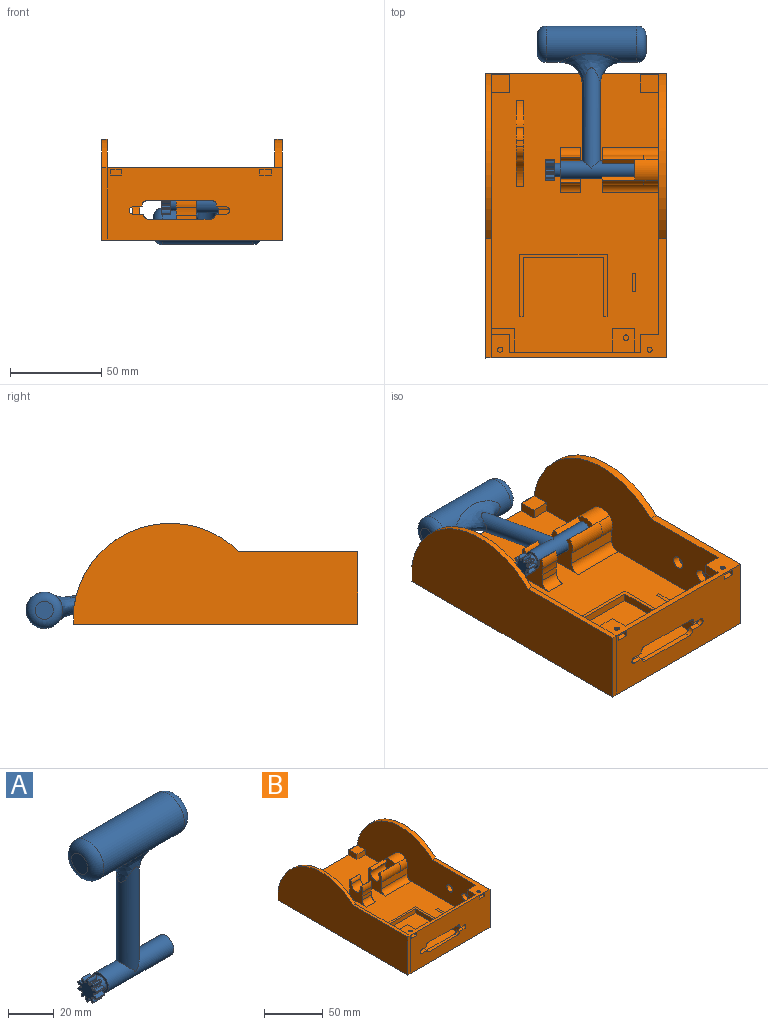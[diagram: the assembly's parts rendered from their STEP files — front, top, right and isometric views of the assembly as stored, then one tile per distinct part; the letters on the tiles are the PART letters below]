
ASSEMBLY  parts=2 mates=1
PART A: 72 faces, bbox 59.7x21.6x87 mm
  f0: cylinder r=5mm len=56.08mm, axis (0,0,-1), area 1528.4mm2, adj f1,f5
  f1: cylinder r=5mm len=40.5mm, axis (-1,0,0), area 1172.3mm2, adj f0,f4,f68
  f2: cylinder r=10mm len=49.7mm, axis (-1,0,0), area 2668.9mm2, adj f5,f70,f71
  f3: plane 10x10mm, normal (1,0,0), area 78.5mm2, adj f71
  f4: plane 10x10mm, normal (-1,0,0), area 34.4mm2, adj f1,f6
  f5: bspline ~34.02x15.67mm, area 649.5mm2, adj f0,f2
  f6: cylinder r=3.75mm len=8.13mm, axis (1,0,0), area 89.7mm2, adj f4,f7,f8,f9,f10,f11,f12,f13
  f7: plane 2.7x2.45mm, normal (1,0,0), area 3.1mm2, adj f6,f21,f40,f42,f45,f47
  f8: plane 2.4x2.01mm, normal (1,0,0), area 3.1mm2, adj f6,f20,f44,f46,f49,f51
  f9: plane 2.7x2.45mm, normal (1,0,0), area 3.1mm2, adj f6,f24,f33,f35,f48,f50
  f10: plane 2.68x2.12mm, normal (1,0,0), area 3.1mm2, adj f6,f26,f29,f31,f32,f34
  f11: plane 2.68x2.12mm, normal (1,0,0), area 3.1mm2, adj f6,f17,f28,f30,f61,f63
  f12: plane 2.7x2.45mm, normal (1,0,0), area 3.1mm2, adj f6,f16,f60,f62,f65,f67
  f13: plane 2.4x2.01mm, normal (1,0,0), area 3.1mm2, adj f6,f19,f53,f55,f64,f66
  f14: plane 2.7x2.45mm, normal (1,0,0), area 3.1mm2, adj f6,f18,f52,f54,f57,f59
  f15: plane 2.68x2.12mm, normal (1,0,0), area 3.1mm2, adj f6,f23,f37,f39,f56,f58
  f16: cylinder r=6mm len=5mm, axis (1,0,0), area 2.9mm2, adj f12,f25,f60,f65
  f17: cylinder r=6mm len=5mm, axis (1,0,0), area 2.9mm2, adj f11,f25,f28,f61
  f18: cylinder r=6mm len=5mm, axis (1,0,0), area 2.9mm2, adj f14,f25,f52,f57
  f19: cylinder r=6mm len=5mm, axis (1,0,0), area 2.9mm2, adj f13,f25,f53,f64
  f20: cylinder r=6mm len=5mm, axis (1,0,0), area 2.9mm2, adj f8,f25,f44,f49
  f21: cylinder r=6mm len=5mm, axis (1,0,0), area 2.9mm2, adj f7,f25,f40,f45
  f22: cylinder r=6mm len=5mm, axis (1,0,0), area 2.9mm2, adj f25,f27,f36,f41
  f23: cylinder r=6mm len=5mm, axis (1,0,0), area 2.9mm2, adj f15,f25,f37,f56
  f24: cylinder r=6mm len=5mm, axis (1,0,0), area 2.9mm2, adj f9,f25,f33,f48
  f25: plane 12.02x11.61mm, normal (-1,0,0), area 75.1mm2, adj f6,f16,f17,f18,f19,f20,f21,f22
  f26: cylinder r=6mm len=5mm, axis (1,0,0), area 2.9mm2, adj f10,f25,f29,f32
  f27: plane 2.68x2.12mm, normal (1,0,0), area 3.1mm2, adj f6,f22,f36,f38,f41,f43
  f28: extruded ~5x1.69mm, area 10.2mm2, adj f11,f17,f25,f30
  f29: extruded ~5x1.69mm, area 10.2mm2, adj f10,f25,f26,f31
  f30: cylinder r=0.41mm len=5mm, axis (1,0,0), area 3mm2, adj f6,f11,f25,f28
  f31: cylinder r=0.41mm len=5mm, axis (1,0,0), area 3mm2, adj f6,f10,f25,f29
  f32: extruded ~5x1.95mm, area 10.2mm2, adj f10,f25,f26,f34
  f33: extruded ~5x1.79mm, area 10.2mm2, adj f9,f24,f25,f35
  f34: cylinder r=0.41mm len=5mm, axis (1,0,0), area 3mm2, adj f6,f10,f25,f32
  f35: cylinder r=0.41mm len=5mm, axis (1,0,0), area 3mm2, adj f6,f9,f25,f33
  f36: extruded ~5x1.69mm, area 10.2mm2, adj f22,f25,f27,f38
  f37: extruded ~5x1.69mm, area 10.2mm2, adj f15,f23,f25,f39
  f38: cylinder r=0.41mm len=5mm, axis (1,0,0), area 3mm2, adj f6,f25,f27,f36
  f39: cylinder r=0.41mm len=5mm, axis (1,0,0), area 3mm2, adj f6,f15,f25,f37
  f40: extruded ~5x1.79mm, area 10.2mm2, adj f7,f21,f25,f42
  f41: extruded ~5x1.95mm, area 10.2mm2, adj f22,f25,f27,f43
  f42: cylinder r=0.41mm len=5mm, axis (1,0,0), area 3mm2, adj f6,f7,f25,f40
  f43: cylinder r=0.41mm len=5mm, axis (1,0,0), area 3mm2, adj f6,f25,f27,f41
  f44: extruded ~5x1.91mm, area 10.2mm2, adj f8,f20,f25,f46
  f45: extruded ~5x1.46mm, area 10.2mm2, adj f7,f21,f25,f47
  f46: cylinder r=0.41mm len=5mm, axis (1,0,0), area 3mm2, adj f6,f8,f25,f44
  f47: cylinder r=0.41mm len=5mm, axis (1,0,0), area 3mm2, adj f6,f7,f25,f45
  f48: extruded ~5x1.46mm, area 10.2mm2, adj f9,f24,f25,f50
  f49: extruded ~5x1.91mm, area 10.2mm2, adj f8,f20,f25,f51
  f50: cylinder r=0.41mm len=5mm, axis (1,0,0), area 3mm2, adj f6,f9,f25,f48
  f51: cylinder r=0.41mm len=5mm, axis (1,0,0), area 3mm2, adj f6,f8,f25,f49
  f52: extruded ~5x1.46mm, area 10.2mm2, adj f14,f18,f25,f54
  f53: extruded ~5x1.91mm, area 10.2mm2, adj f13,f19,f25,f55
  f54: cylinder r=0.41mm len=5mm, axis (1,0,0), area 3mm2, adj f6,f14,f25,f52
  f55: cylinder r=0.41mm len=5mm, axis (1,0,0), area 3mm2, adj f6,f13,f25,f53
  f56: extruded ~5x1.95mm, area 10.2mm2, adj f15,f23,f25,f58
  f57: extruded ~5x1.79mm, area 10.2mm2, adj f14,f18,f25,f59
  f58: cylinder r=0.41mm len=5mm, axis (1,0,0), area 3mm2, adj f6,f15,f25,f56
  f59: cylinder r=0.41mm len=5mm, axis (1,0,0), area 3mm2, adj f6,f14,f25,f57
  f60: extruded ~5x1.79mm, area 10.2mm2, adj f12,f16,f25,f62
  f61: extruded ~5x1.95mm, area 10.2mm2, adj f11,f17,f25,f63
  f62: cylinder r=0.41mm len=5mm, axis (1,0,0), area 3mm2, adj f6,f12,f25,f60
  f63: cylinder r=0.41mm len=5mm, axis (1,0,0), area 3mm2, adj f6,f11,f25,f61
  f64: extruded ~5x1.91mm, area 10.2mm2, adj f13,f19,f25,f66
  f65: extruded ~5x1.46mm, area 10.2mm2, adj f12,f16,f25,f67
  f66: cylinder r=0.41mm len=5mm, axis (1,0,0), area 3mm2, adj f6,f13,f25,f64
  f67: cylinder r=0.41mm len=5mm, axis (1,0,0), area 3mm2, adj f6,f12,f25,f65
  f68: plane 10x10mm, normal (1,0,0), area 78.5mm2, adj f1
  f69: plane 10x10mm, normal (-1,0,0), area 78.5mm2, adj f70
  f70: torus R=5mm, axis (1,0,0), area 403.8mm2, adj f2,f69
  f71: torus R=5mm, axis (1,0,0), area 403.8mm2, adj f2,f3
PART B: 146 faces, bbox 99.2x155.8x55.3 mm
  f0: plane 96.21x39.7mm, normal (0,-1,0), area 3329.3mm2, adj f3,f4,f18,f37,f56,f57,f58,f59
  f1: plane 152.74x50.32mm, normal (-1,0,0), area 5424.2mm2, adj f2,f15,f20,f21,f22,f23,f24,f25
  f2: plane 91.94x34.7mm, normal (0,1,0), area 2463.3mm2, adj f1,f16,f37,f56,f57,f58,f59,f60
  f3: plane 11x3mm, normal (-1,0,0), area 33mm2, adj f0,f90,f141,f145
  f4: plane 11x3mm, normal (-1,0,0), area 33mm2, adj f0,f89,f140,f144
  f5: plane 155.76x55.32mm, normal (-1,0,0), area 6830mm2, adj f68,f69,f70,f71,f97,f136
  f6: plane 24.89x19.22mm, normal (1,0,0), area 214.8mm2, adj f7,f8,f17,f28,f29,f40,f41,f119
  f7: cylinder r=8.15mm len=11mm, axis (-1,0,0), area 69mm2, adj f6,f9,f127,f131
  f8: cylinder r=5.15mm len=11mm, axis (-1,0,0), area 188.3mm2, adj f6,f9,f128,f129
  f9: plane 24.89x19.22mm, normal (-1,0,0), area 214.8mm2, adj f7,f8,f17,f28,f29,f40,f41,f119
  f10: plane 10.2x3.5mm, normal (-1,0,0), area 35.7mm2, adj f116,f118,f119,f123
  f11: plane 10.2x3.5mm, normal (1,0,0), area 35.7mm2, adj f116,f118,f119,f123
  f12: plane 6.6x3.5mm, normal (0,1,0), area 23.1mm2, adj f119,f120,f121,f122
  f13: plane 12.95x6.5mm, normal (0,1,0), area 61.1mm2, adj f16,f102,f103,f119,f120,f121,f122
  f14: plane 10x5.5mm, normal (0,1,0), area 55mm2, adj f16,f37,f76,f142
  f15: plane 10x5.5mm, normal (0,1,0), area 55mm2, adj f1,f37,f77,f143
  f16: plane 152.73x50.32mm, normal (1,0,0), area 5755mm2, adj f2,f13,f14,f68,f70,f75,f103,f119
  f17: cylinder r=8.15mm len=11mm, axis (-1,0,0), area 69mm2, adj f6,f9,f126,f130
  f18: plane 155.76x55.32mm, normal (1,0,0), area 6753.1mm2, adj f0,f36,f37,f42,f43,f71,f97
  f19: plane 4x3mm, normal (0,0,1), area 12mm2, adj f50,f51,f54,f55
  f20: cylinder r=9mm len=13.11mm, axis (-1,0,0), area 163.9mm2, adj f1,f21,f22,f30,f31,f38
  f21: cylinder r=8.1mm len=9.08mm, axis (-1,0,0), area 79.7mm2, adj f1,f20,f23,f39
  f22: cylinder r=8.2mm len=9.08mm, axis (-1,0,0), area 79.5mm2, adj f1,f20,f24,f27
  f23: plane 30.94x6.68mm, normal (0,1,0), area 206.7mm2, adj f1,f21,f25,f31,f35
  f24: plane 30.94x6.68mm, normal (0,-1,0), area 206.7mm2, adj f1,f22,f26,f30,f35
  f25: cylinder r=5mm len=30.94mm, axis (1,0,0), area 243mm2, adj f1,f23,f35,f119
  f26: cylinder r=5mm len=30.94mm, axis (-1,0,0), area 243mm2, adj f1,f24,f35,f119
  f27: plane 9.08x2.39mm, normal (1,0,0), area 0.1mm2, adj f22,f30
  f28: plane 11x3.73mm, normal (0,-1,0), area 41.1mm2, adj f6,f9,f40,f130
  f29: plane 11x3.73mm, normal (0,1,0), area 41.1mm2, adj f6,f9,f41,f131
  f30: cylinder r=8.15mm len=22.84mm, axis (-1,0,0), area 224.3mm2, adj f20,f24,f27,f34,f35
  f31: cylinder r=8.15mm len=22.84mm, axis (-1,0,0), area 224.3mm2, adj f20,f23,f32,f35,f39
  f32: plane 17.84x2.12mm, normal (0,-0.71,0.71), area 53.5mm2, adj f31,f33,f35,f38
  f33: cylinder r=5.15mm len=17.84mm, axis (-1,0,0), area 432.9mm2, adj f32,f34,f35,f38
  f34: plane 17.84x2.12mm, normal (0,0.71,0.71), area 53.5mm2, adj f30,f33,f35,f38
  f35: plane 24.89x20.76mm, normal (-1,0,0), area 226.9mm2, adj f23,f24,f25,f26,f30,f31,f32,f33
  f36: cylinder r=53.32mm len=90.46mm, axis (1,0,0), area 502.6mm2, adj f1,f18,f37,f71,f132
  f37: plane 96.21x65.3mm, normal (0,0,1), area 741.9mm2, adj f0,f1,f2,f14,f15,f18,f36,f70
  f38: plane 13x11.53mm, normal (-1,0,0), area 112.2mm2, adj f20,f32,f33,f34
  f39: plane 9.08x2.4mm, normal (-1,0,0), area 0.1mm2, adj f21,f31
  f40: cylinder r=5mm len=11mm, axis (-1,0,0), area 86.4mm2, adj f6,f9,f28,f119
  f41: cylinder r=5mm len=11mm, axis (1,0,0), area 86.4mm2, adj f6,f9,f29,f119
  f42: cylinder r=3.5mm len=7mm, axis (1,0,0), area 93.8mm2, adj f1,f18
  f43: cylinder r=3.5mm len=7mm, axis (1,0,0), area 93.8mm2, adj f1,f18
  f44: plane 9x4mm, normal (0,1,0), area 36mm2, adj f50,f52,f54,f55
  f45: plane 9x4mm, normal (0,-1,0), area 36mm2, adj f51,f53,f54,f55
  f46: cylinder r=4.05mm len=8.1mm, axis (1,0,0), area 50.9mm2, adj f47,f49,f54,f55
  f47: plane 16x4mm, normal (0,-1,0), area 64mm2, adj f46,f48,f54,f55
  f48: cylinder r=4.05mm len=8.1mm, axis (1,0,0), area 50.9mm2, adj f47,f49,f54,f55
  f49: plane 16x4mm, normal (0,1,0), area 64mm2, adj f46,f48,f54,f55
  f50: cylinder r=7mm len=7mm, axis (1,0,0), area 44mm2, adj f19,f44,f54,f55
  f51: cylinder r=7mm len=7mm, axis (-1,0,0), area 44mm2, adj f19,f45,f54,f55
  f52: cylinder r=15mm len=15mm, axis (-1,0,0), area 94.2mm2, adj f44,f54,f55,f119
  f53: cylinder r=15mm len=15mm, axis (1,0,0), area 94.2mm2, adj f45,f54,f55,f119
  f54: plane 47x31mm, normal (1,0,0), area 421.4mm2, adj f19,f44,f45,f46,f47,f48,f49,f50
  f55: plane 47x31mm, normal (-1,0,0), area 421.4mm2, adj f19,f44,f45,f46,f47,f48,f49,f50
  f56: plane 36.58x3mm, normal (0,0,-1), area 109.7mm2, adj f0,f2,f98,f99
  f57: plane 3x1.08mm, normal (-1,0,0.1), area 3.3mm2, adj f0,f2,f58,f98
  f58: plane 5.71x3mm, normal (0,0,-1), area 17.1mm2, adj f0,f2,f57,f59
  f59: cylinder r=2mm len=3.99mm, axis (0,1,0), area 18.9mm2, adj f0,f2,f58,f60
  f60: plane 5.5x3mm, normal (0,0,1), area 16.5mm2, adj f0,f2,f59,f61
  f61: plane 3x0.07mm, normal (-1,0,0.1), area 0.2mm2, adj f0,f2,f60,f100
  f62: plane 33.57x3mm, normal (0,0,1), area 100.7mm2, adj f0,f2,f100,f101
  f63: plane 3x0.07mm, normal (1,0,0.1), area 0.2mm2, adj f0,f2,f64,f101
  f64: plane 5.5x3mm, normal (0,0,1), area 16.5mm2, adj f0,f2,f63,f65
  f65: cylinder r=2mm len=3.99mm, axis (0,1,0), area 18.9mm2, adj f0,f2,f64,f66
  f66: plane 5.71x3mm, normal (0,0,-1), area 17.1mm2, adj f0,f2,f65,f67
  f67: plane 3x1.05mm, normal (1,0,0.1), area 3.2mm2, adj f0,f2,f66,f99
  f68: cylinder r=53.32mm len=90.46mm, axis (1,0,0), area 353.7mm2, adj f5,f16,f70,f134,f136
  f69: plane 39.7x3mm, normal (0,-1,0), area 119.1mm2, adj f0,f5,f70,f97
  f70: plane 65.3x3mm, normal (0,0,1), area 195.9mm2, adj f5,f16,f37,f68,f69
  f71: plane 99.21x9.71mm, normal (0,1,0), area 612.1mm2, adj f5,f18,f36,f72,f74,f95,f96,f97
  f72: plane 10x5.21mm, normal (-1,0,0), area 52mm2, adj f71,f73,f119,f133,f138
  f73: plane 10x5.21mm, normal (0,-1,0), area 52.1mm2, adj f1,f72,f119,f133
  f74: plane 10x5.21mm, normal (1,0,0), area 52mm2, adj f71,f75,f119,f135,f137
  f75: plane 10x5.21mm, normal (0,-1,0), area 52.1mm2, adj f16,f74,f119,f135
  f76: plane 10x5.5mm, normal (1,0,0), area 55mm2, adj f2,f14,f37,f142
  f77: plane 10x5.5mm, normal (-1,0,0), area 55mm2, adj f2,f15,f37,f143
  f78: plane 11x3mm, normal (1,0,0), area 33mm2, adj f0,f90,f141,f145
  f79: plane 11x3mm, normal (1,0,0), area 33mm2, adj f0,f89,f139,f144
  f80: plane 8.71x3.21mm, normal (0,-1,0), area 24.8mm2, adj f81,f84,f91,f96,f97
  f81: plane 8.71x3.2mm, normal (0,-1,0), area 24.8mm2, adj f80,f82,f91,f96,f97
  f82: plane 8.71x2.99mm, normal (1,0,0), area 26.1mm2, adj f81,f83,f91,f97
  f83: plane 8.71x6.4mm, normal (0,1,0), area 55.7mm2, adj f82,f84,f91,f97
  f84: plane 8.71x3mm, normal (-1,0,0), area 26.1mm2, adj f80,f83,f91,f97
  f85: plane 8.71x6.4mm, normal (0,-1,0), area 49.6mm2, adj f86,f88,f92,f95,f97
  f86: plane 8.71x3mm, normal (1,0,0), area 26.1mm2, adj f85,f87,f92,f97
  f87: plane 8.71x6.4mm, normal (0,1,0), area 55.7mm2, adj f86,f88,f92,f97
  f88: plane 8.71x3mm, normal (-1,0,0), area 26.1mm2, adj f85,f87,f92,f97
  f89: plane 6.4x3mm, normal (0,-1,0), area 19.2mm2, adj f4,f79,f139,f140,f144
  f90: plane 6.4x3mm, normal (0,-1,0), area 19.2mm2, adj f3,f78,f141,f145
  f91: plane 6.4x3mm, normal (0,0,-1), area 19.2mm2, adj f80,f81,f82,f83,f84
  f92: plane 6.4x3mm, normal (0,0,-1), area 19.2mm2, adj f85,f86,f87,f88
  f93: cylinder r=1.4mm len=2.8mm, axis (0,0,1), area 8.8mm2, adj f37,f139,f140
  f94: cylinder r=1.4mm len=2.8mm, axis (0,0,1), area 8.8mm2, adj f37,f141
  f95: cylinder r=1.4mm len=3.5mm, axis (0,1,0), area 30.8mm2, adj f71,f85
  f96: cylinder r=1.4mm len=3.52mm, axis (0,1,0), area 31mm2, adj f71,f80,f81
  f97: plane 155.76x99.21mm, normal (0,0,-1), area 15413.8mm2, adj f0,f5,f18,f69,f71,f80,f81,f82
  f98: cylinder r=2mm len=3mm, axis (0,-1,0), area 10mm2, adj f0,f2,f56,f57
  f99: cylinder r=2mm len=3mm, axis (0,1,0), area 10mm2, adj f0,f2,f56,f67
  f100: cylinder r=3mm len=3mm, axis (0,1,0), area 13.2mm2, adj f0,f2,f61,f62
  f101: cylinder r=3mm len=3mm, axis (0,-1,0), area 13.2mm2, adj f0,f2,f62,f63
  f102: plane 13.1x6.5mm, normal (1,0,0), area 85.1mm2, adj f2,f13,f103,f119
  f103: plane 13.1x12.95mm, normal (0,0,1), area 162.6mm2, adj f2,f13,f16,f102,f125
  f104: plane 13.1x6.5mm, normal (-1,0,0), area 85.1mm2, adj f2,f105,f116,f119
  f105: plane 13.1x12.5mm, normal (0,0,1), area 156.7mm2, adj f2,f104,f116,f117,f124
  f106: plane 34x4.3mm, normal (-1,0,0), area 146.2mm2, adj f107,f113,f114,f119
  f107: plane 4.3x2mm, normal (0,-1,0), area 8.6mm2, adj f106,f108,f114,f119
  f108: plane 32x4.3mm, normal (1,0,0), area 137.6mm2, adj f107,f109,f114,f119
  f109: plane 44x4.3mm, normal (0,-1,0), area 189.2mm2, adj f108,f110,f114,f119
  f110: plane 32x4.3mm, normal (-1,0,0), area 137.6mm2, adj f109,f111,f114,f119
  f111: plane 4.3x2mm, normal (0,-1,0), area 8.6mm2, adj f110,f112,f114,f119
  f112: plane 34x4.3mm, normal (1,0,0), area 146.2mm2, adj f111,f113,f114,f119
  f113: plane 48x4.3mm, normal (0,1,0), area 206.4mm2, adj f106,f112,f114,f119
  f114: plane 48x34mm, normal (0,0,1), area 224mm2, adj f106,f107,f108,f109,f110,f111,f112,f113
  f115: plane 10x2mm, normal (0,0,1), area 20mm2, adj f119
  f116: plane 12.5x6.5mm, normal (0,1,0), area 58.2mm2, adj f10,f11,f104,f105,f117,f119,f123
  f117: plane 13.1x6.5mm, normal (1,0,0), area 85.1mm2, adj f2,f105,f116,f119
  f118: plane 6.6x3.5mm, normal (0,1,0), area 23.1mm2, adj f10,f11,f119,f123
  f119: plane 152.76x91.94mm, normal (0,0,1), area 12169.3mm2, adj f1,f2,f6,f9,f10,f11,f12,f13
  f120: plane 10.05x3.5mm, normal (1,0,0), area 35.2mm2, adj f12,f13,f119,f122
  f121: plane 10.05x3.5mm, normal (-1,0,0), area 35.2mm2, adj f12,f13,f119,f122
  f122: plane 10.05x6.6mm, normal (0,0,-1), area 59.3mm2, adj f12,f13,f120,f121,f125
  f123: plane 10.2x6.6mm, normal (0,0,-1), area 60.2mm2, adj f10,f11,f116,f118,f124
  f124: cylinder r=1.5mm len=3mm, axis (0,0,1), area 28.3mm2, adj f105,f123
  f125: cylinder r=1.5mm len=3mm, axis (0,0,1), area 28.3mm2, adj f103,f122
  f126: plane 11x0.22mm, normal (0,0.59,0.81), area 3.1mm2, adj f6,f9,f17,f128
  f127: plane 11x0.22mm, normal (0,-0.59,0.81), area 3.1mm2, adj f6,f7,f9,f129
  f128: cylinder r=4mm len=11mm, axis (-1,0,0), area 45.3mm2, adj f6,f8,f9,f126
  f129: cylinder r=4mm len=11mm, axis (-1,0,0), area 45.3mm2, adj f6,f8,f9,f127
  f130: cylinder r=20mm len=11mm, axis (-1,0,0), area 49.4mm2, adj f6,f9,f17,f28
  f131: cylinder r=20mm len=11mm, axis (-1,0,0), area 49.4mm2, adj f6,f7,f9,f29
  f132: plane 0.14x0.02mm, normal (1,0,0), area 0mm2, adj f36,f138
  f133: plane 10x9.5mm, normal (0,0,1), area 95mm2, adj f1,f72,f73,f138
  f134: plane 0.15x0.02mm, normal (-1,0,0), area 0mm2, adj f68,f137
  f135: plane 10x9.5mm, normal (0,0,1), area 95mm2, adj f16,f74,f75,f137
  f136: plane 3x0mm, normal (0,-0.14,0.99), area 0mm2, adj f5,f68,f71
  f137: cylinder r=0.5mm len=10mm, axis (-1,0,0), area 7.9mm2, adj f16,f71,f74,f134,f135
  f138: cylinder r=0.5mm len=10mm, axis (-1,0,0), area 7.9mm2, adj f1,f71,f72,f132,f133
  f139: plane 11x3.2mm, normal (0,0,-1), area 32.1mm2, adj f0,f79,f89,f93,f140
  f140: plane 11x3.2mm, normal (0,0,-1), area 32.1mm2, adj f0,f4,f89,f93,f139
  f141: plane 11x6.4mm, normal (0,0,-1), area 64.2mm2, adj f0,f3,f78,f90,f94
  f142: plane 10x10mm, normal (0,0,-1), area 100mm2, adj f2,f14,f16,f76
  f143: plane 10x10mm, normal (0,0,-1), area 100mm2, adj f1,f2,f15,f77
  f144: plane 11x6.4mm, normal (0,0,1), area 70.4mm2, adj f0,f4,f79,f89
  f145: plane 11x6.4mm, normal (0,0,1), area 70.4mm2, adj f0,f3,f78,f90
PLACE A rot(axis=(-1,0,0),100.2deg) t=(-7.78,-57.22,32.14)mm
PLACE B t=(-7.78,-39.62,10.98)mm
MATE revolute A.f6 <-> B.f8  axis (-1,0,0) through (-34.78,-39.62,28.98)mm
